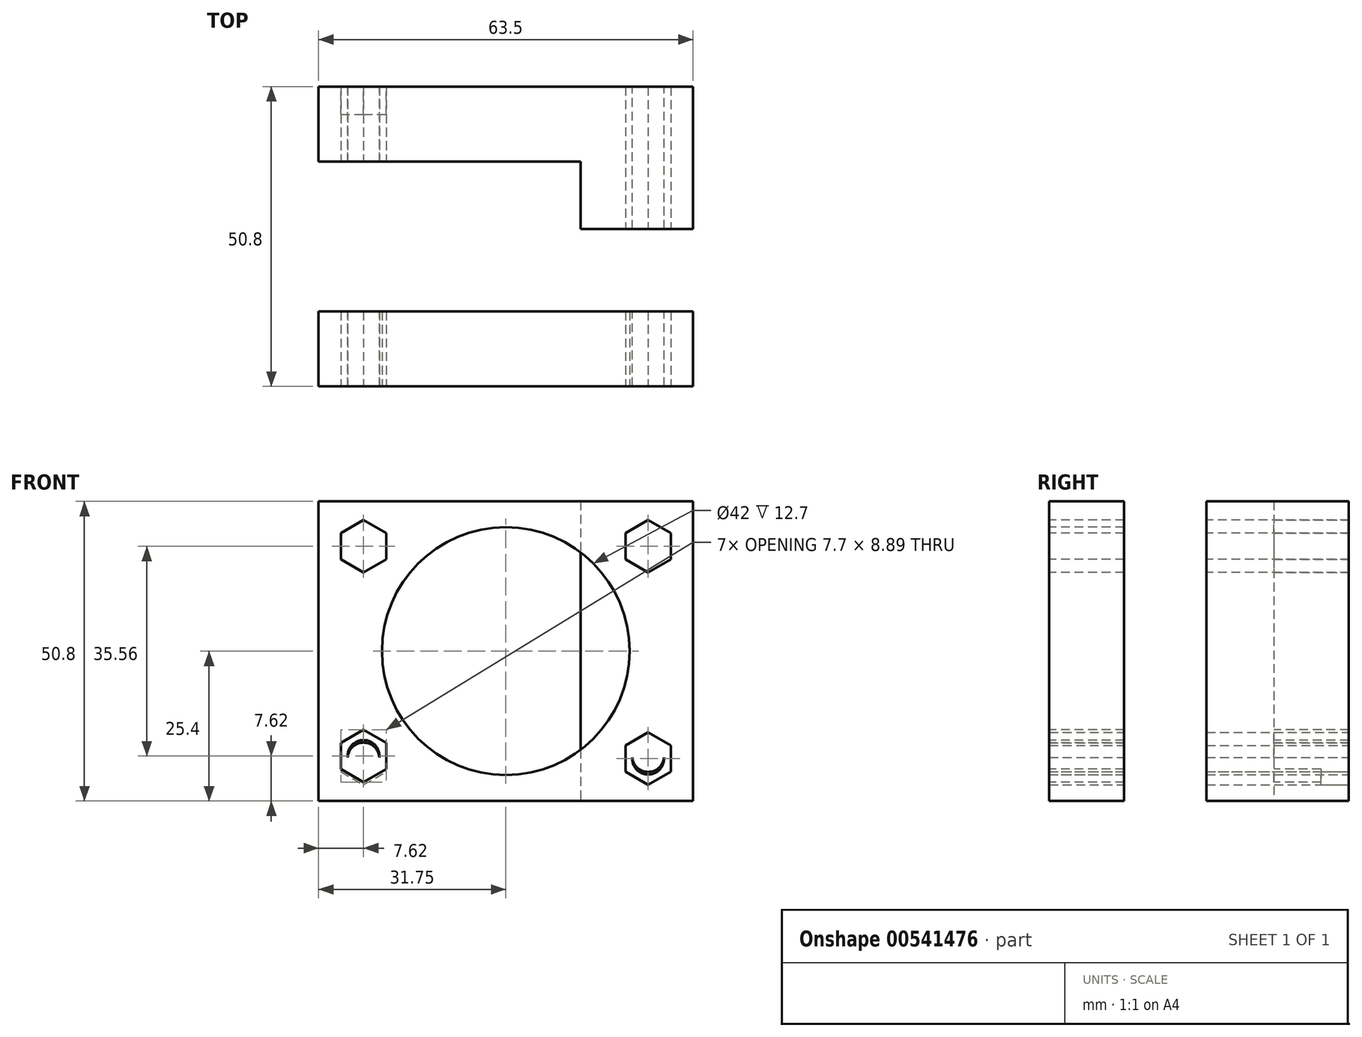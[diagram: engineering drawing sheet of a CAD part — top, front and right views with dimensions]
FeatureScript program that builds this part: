
annotation { "Feature Type Name" : "Feature", "Feature Type Description" : "" }
export const myFeature = defineFeature(function(context is Context, id is Id, definition is map)
    precondition{}
    {
        {
            var Q0;
            Q0=qCreatedBy(makeId("Top.planeOp"),FACE);
            var sketch = newSketch(context, id + "F0", { "sketchPlane" : qUnion([Q0])});
            skLineSegment(sketch, "E0.bottom", {"start": v(0, 0) * mm, "end": v(63.5, 0) * mm});
            skLineSegment(sketch, "E0.top", {"start": v(0, 12.7) * mm, "end": v(63.5, 12.7) * mm});
            skLineSegment(sketch, "E0.left", {"start": v(0, 0) * mm, "end": v(0, 12.7) * mm});
            skLineSegment(sketch, "E0.right", {"start": v(63.5, 0) * mm, "end": v(63.5, 12.7) * mm});
            skLineSegment(sketch, "E1.bottom", {"start": v(0, 12.7) * mm, "end": v(19.05, 12.7) * mm});
            skLineSegment(sketch, "E1.top", {"start": v(0, 24.13) * mm, "end": v(19.05, 24.13) * mm});
            skLineSegment(sketch, "E1.left", {"start": v(0, 12.7) * mm, "end": v(0, 24.13) * mm});
            skLineSegment(sketch, "E1.right", {"start": v(19.05, 12.7) * mm, "end": v(19.05, 24.13) * mm});
            skLineSegment(sketch, "E2.bottom", {"start": v(63.5, 12.7) * mm, "end": v(44.45, 12.7) * mm});
            skLineSegment(sketch, "E2.top", {"start": v(63.5, 24.13) * mm, "end": v(44.45, 24.13) * mm});
            skLineSegment(sketch, "E2.left", {"start": v(63.5, 12.7) * mm, "end": v(63.5, 24.13) * mm});
            skLineSegment(sketch, "E2.right", {"start": v(44.45, 12.7) * mm, "end": v(44.45, 24.13) * mm});
            skLineSegment(sketch, "E3", {"start": v(25.4, 25.4) * mm, "end": v(0, 25.4) * mm});
            skLineSegment(sketch, "E4.MirrorCS", {"start": v(0, 50.8) * mm, "end": v(0, 38.1) * mm});
            skLineSegment(sketch, "E5.MirrorCS", {"start": v(44.45, 38.1) * mm, "end": v(44.45, 26.67) * mm});
            skLineSegment(sketch, "E6.MirrorCS", {"start": v(63.5, 38.1) * mm, "end": v(63.5, 26.67) * mm});
            skLineSegment(sketch, "E7.MirrorCS", {"start": v(63.5, 26.67) * mm, "end": v(44.45, 26.67) * mm});
            skLineSegment(sketch, "E8.MirrorCS", {"start": v(63.5, 38.1) * mm, "end": v(44.45, 38.1) * mm});
            skLineSegment(sketch, "E9.MirrorCS", {"start": v(0, 50.8) * mm, "end": v(63.5, 50.8) * mm});
            skLineSegment(sketch, "E10.MirrorCS", {"start": v(0, 38.1) * mm, "end": v(63.5, 38.1) * mm});
            skLineSegment(sketch, "E11.MirrorCS", {"start": v(63.5, 50.8) * mm, "end": v(63.5, 38.1) * mm});
            skLineSegment(sketch, "E12.MirrorCS", {"start": v(0, 38.1) * mm, "end": v(19.05, 38.1) * mm});
            skLineSegment(sketch, "E13.MirrorCS", {"start": v(0, 26.67) * mm, "end": v(19.05, 26.67) * mm});
            skLineSegment(sketch, "E14.MirrorCS", {"start": v(0, 38.1) * mm, "end": v(0, 26.67) * mm});
            skLineSegment(sketch, "E15.MirrorCS", {"start": v(19.05, 38.1) * mm, "end": v(19.05, 26.67) * mm});
            skPoint(sketch, "E16.orphan", {"position": v(25.4, 25.4) * mm});
            skPoint(sketch, "E17.MirrorCS.start.orphan", {"position": v(31.75, 50.8) * mm});
            skPoint(sketch, "E18.start.orphan", {"position": v(31.75, 0) * mm});
            skSolve(sketch);
        }
        {
            var Q0;
            Q0=makeQuery(id+"F0.imprint","IMPRINT",FACE,{"disambiguationData":[TD([[makeQuery(id+"F0.imprint","IMPRINT",EDGE,{"derivedFrom":sQuery(id+"F0.wireOp",EDGE,"E4.MirrorCS")}),1.0]])]});
            var Q1;
            Q1=makeQuery(id+"F0.imprint","IMPRINT",FACE,{"disambiguationData":[TD([[makeQuery(id+"F0.imprint","IMPRINT",EDGE,{"derivedFrom":sQuery(id+"F0.wireOp",EDGE,"E12.MirrorCS")}),-1.0]])]});
            var Q2;
            {var subQ0=sQuery(id+"F0.wireOp",EDGE,"E5.MirrorCS");Q2=makeQuery(id+"F0.imprint","IMPRINT",FACE,{"disambiguationData":[TD([[makeQuery(id+"F0.imprint","IMPRINT",EDGE,{"derivedFrom":subQ0}),1.0]])]});}
            var Q3;
            Q3=makeQuery(id+"F0.imprint","IMPRINT",FACE,{"disambiguationData":[TD([[makeQuery(id+"F0.imprint","IMPRINT",EDGE,{"derivedFrom":sQuery(id+"F0.wireOp",EDGE,"E2.bottom")}),-1.0]])]});
            var Q4;
            Q4=makeQuery(id+"F0.imprint","IMPRINT",FACE,{"disambiguationData":[TD([[makeQuery(id+"F0.imprint","IMPRINT",EDGE,{"derivedFrom":sQuery(id+"F0.wireOp",EDGE,"E0.bottom")}),1.0]])]});
            var Q5;
            Q5=makeQuery(id+"F0.imprint","IMPRINT",FACE,{"disambiguationData":[TD([[makeQuery(id+"F0.imprint","IMPRINT",EDGE,{"derivedFrom":sQuery(id+"F0.wireOp",EDGE,"E1.bottom")}),1.0]])]});
            extrude(context, id + "F1", {"entities" : qUnion([Q0, Q1, Q2, Q3, Q4, Q5]), "depth" : 50.8 * mm, "offsetDistance" : 25.4 * mm});
        }
        {
            var Q0;
            Q0=makeQuery(id+"F1.opExtrude","SWEPT_FACE",FACE,{"disambiguationData":[OSD([sQuery(id+"F0.wireOp",EDGE,"E0.bottom")])]});
            var sketch = newSketch(context, id + "F2", { "sketchPlane" : qUnion([Q0])});
            skCircle(sketch, "E19", {"center": v(31.75, 25.4) * mm, "radius": 21 * mm});
            skPoint(sketch, "E19.centerSnap0", {"position": v(0, 25.4) * mm});
            skPoint(sketch, "E19.centerSnap1", {"position": v(31.75, 50.8) * mm});
            skLineSegment(sketch, "E20", {"start": v(0, 50.8) * mm, "end": v(7.62, 50.8) * mm});
            skLineSegment(sketch, "E21", {"start": v(0, 50.8) * mm, "end": v(0, 43.18) * mm});
            skCircle(sketch, "E22", {"center": v(7.62, 43.18) * mm, "radius": 2.7 * mm});
            skLineSegment(sketch, "E23", {"start": v(7.62, 43.18) * mm, "end": v(7.62, 38.74) * mm});
            skCircle(sketch, "E24.cCircle", {"center": v(7.62, 43.18) * mm, "radius": 4.44 * mm, "construction": true});
            skLineSegment(sketch, "E24.0", {"start": v(7.62, 38.74) * mm, "end": v(3.77, 40.96) * mm});
            skLineSegment(sketch, "E24.1", {"start": v(3.77, 40.96) * mm, "end": v(3.77, 45.4) * mm});
            skLineSegment(sketch, "E24.2", {"start": v(3.77, 45.4) * mm, "end": v(7.62, 47.62) * mm});
            skLineSegment(sketch, "E24.3", {"start": v(7.62, 47.62) * mm, "end": v(11.47, 45.4) * mm});
            skLineSegment(sketch, "E24.4", {"start": v(11.47, 45.4) * mm, "end": v(11.47, 40.96) * mm});
            skLineSegment(sketch, "E24.5", {"start": v(11.47, 40.96) * mm, "end": v(7.62, 38.74) * mm});
            skLineSegment(sketch, "E25", {"start": v(0, 25.4) * mm, "end": v(2.5, 25.4) * mm});
            skLineSegment(sketch, "E26", {"start": v(31.75, 50.8) * mm, "end": v(31.75, 48.56) * mm});
            skLineSegment(sketch, "E27.MirrorCS", {"start": v(3.77, 5.4) * mm, "end": v(7.62, 3.18) * mm});
            skLineSegment(sketch, "E28.MirrorCS", {"start": v(7.62, 12.07) * mm, "end": v(3.77, 9.84) * mm});
            skCircle(sketch, "E29.MirrorC", {"center": v(7.62, 7.62) * mm, "radius": 2.7 * mm});
            skLineSegment(sketch, "E30.MirrorCS", {"start": v(11.47, 9.84) * mm, "end": v(7.62, 12.07) * mm});
            skLineSegment(sketch, "E31.MirrorCS", {"start": v(7.62, 3.18) * mm, "end": v(11.47, 5.4) * mm});
            skCircle(sketch, "E32.MirrorC", {"center": v(7.62, 7.62) * mm, "radius": 4.44 * mm, "construction": true});
            skLineSegment(sketch, "E33.MirrorCS", {"start": v(7.62, 7.62) * mm, "end": v(7.62, 12.07) * mm});
            skLineSegment(sketch, "E34.MirrorCS", {"start": v(11.47, 5.4) * mm, "end": v(11.47, 9.84) * mm});
            skLineSegment(sketch, "E35.MirrorCS", {"start": v(3.77, 9.84) * mm, "end": v(3.77, 5.4) * mm});
            skLineSegment(sketch, "E36.MirrorCS", {"start": v(59.73, 45.4) * mm, "end": v(55.88, 47.62) * mm});
            skLineSegment(sketch, "E37.MirrorCS", {"start": v(55.88, 38.74) * mm, "end": v(59.73, 40.96) * mm});
            skCircle(sketch, "E38.MirrorC", {"center": v(55.88, 43.18) * mm, "radius": 4.44 * mm, "construction": true});
            skLineSegment(sketch, "E39.MirrorCS", {"start": v(55.88, 43.18) * mm, "end": v(55.88, 38.74) * mm});
            skCircle(sketch, "E40.MirrorC", {"center": v(55.88, 43.18) * mm, "radius": 2.7 * mm});
            skLineSegment(sketch, "E41.MirrorCS", {"start": v(59.73, 40.96) * mm, "end": v(59.73, 45.4) * mm});
            skLineSegment(sketch, "E42.MirrorCS", {"start": v(55.88, 47.62) * mm, "end": v(52.03, 45.4) * mm});
            skLineSegment(sketch, "E43.MirrorCS", {"start": v(52.03, 40.96) * mm, "end": v(55.88, 38.74) * mm});
            skLineSegment(sketch, "E44.MirrorCS", {"start": v(55.88, 3.18) * mm, "end": v(52.03, 5.4) * mm});
            skLineSegment(sketch, "E45.MirrorCS", {"start": v(55.88, 12.07) * mm, "end": v(59.73, 9.84) * mm});
            skCircle(sketch, "E46.MirrorC", {"center": v(55.88, 7.62) * mm, "radius": 2.7 * mm});
            skLineSegment(sketch, "E47.MirrorCS", {"start": v(59.73, 5.4) * mm, "end": v(55.88, 3.18) * mm});
            skLineSegment(sketch, "E48.MirrorCS", {"start": v(52.03, 9.84) * mm, "end": v(55.88, 12.07) * mm});
            skCircle(sketch, "E49.MirrorC", {"center": v(55.88, 7.62) * mm, "radius": 4.44 * mm, "construction": true});
            skLineSegment(sketch, "E50.MirrorCS", {"start": v(55.88, 7.62) * mm, "end": v(55.88, 12.07) * mm});
            skLineSegment(sketch, "E51.MirrorCS", {"start": v(59.73, 9.84) * mm, "end": v(59.73, 5.4) * mm});
            skLineSegment(sketch, "E52.MirrorCS", {"start": v(52.03, 5.4) * mm, "end": v(52.03, 9.84) * mm});
            skLineSegment(sketch, "E53.MirrorCS", {"start": v(52.03, 45.4) * mm, "end": v(52.03, 40.96) * mm});
            skSolve(sketch);
        }
        {
            var Q0;
            Q0=makeQuery(id+"F2.imprint","IMPRINT",FACE,{"disambiguationData":[TD([[makeQuery(id+"F2.imprint","IMPRINT",EDGE,{"derivedFrom":sQuery(id+"F2.wireOp",EDGE,"E22")}),1.0]])]});
            var Q1;
            Q1=makeQuery(id+"F2.imprint","IMPRINT",FACE,{"disambiguationData":[TD([[makeQuery(id+"F2.imprint","IMPRINT",EDGE,{"derivedFrom":sQuery(id+"F2.wireOp",EDGE,"E29.MirrorC")}),-1.0]])]});
            var Q2;
            Q2=makeQuery(id+"F2.imprint","IMPRINT",FACE,{"disambiguationData":[TD([[makeQuery(id+"F2.imprint","IMPRINT",EDGE,{"derivedFrom":sQuery(id+"F2.wireOp",EDGE,"E46.MirrorC")}),1.0]])]});
            var Q3;
            Q3=makeQuery(id+"F2.imprint","IMPRINT",FACE,{"disambiguationData":[TD([[makeQuery(id+"F2.imprint","IMPRINT",EDGE,{"derivedFrom":sQuery(id+"F2.wireOp",EDGE,"E40.MirrorC")}),-1.0]])]});
            extrude(context, id + "F3", {"entities" : qUnion([Q0, Q1, Q2, Q3]), "operationType" : NewBodyOperationType.REMOVE, "oppositeDirection" : true, "depth" : 50.8 * mm, "offsetDistance" : 25.4 * mm});
        }
        {
            var Q0;
            Q0=makeQuery(id+"F2.imprint","IMPRINT",FACE,{"disambiguationData":[TD([[makeQuery(id+"F2.imprint","IMPRINT",EDGE,{"derivedFrom":sQuery(id+"F2.wireOp",EDGE,"E19")}),1.0]])]});
            extrude(context, id + "F4", {"entities" : qUnion([Q0]), "operationType" : NewBodyOperationType.REMOVE, "oppositeDirection" : true, "depth" : 12.7 * mm, "offsetDistance" : 25.4 * mm});
        }
        {
            var Q0;
            Q0=makeQuery(id+"F1.opExtrude","SWEPT_FACE",FACE,{"disambiguationData":[OSD([sQuery(id+"F0.wireOp",EDGE,"E9.MirrorCS")])]});
            var sketch = newSketch(context, id + "F5", { "sketchPlane" : qUnion([Q0])});
            skCircle(sketch, "E54", {"center": v(-31.75, 25.18) * mm, "radius": 21 * mm});
            skPoint(sketch, "E54.centerSnap0", {"position": v(-68.13, 25.18) * mm});
            skPoint(sketch, "E54.centerSnap1", {"position": v(-31.75, 50.8) * mm});
            skLineSegment(sketch, "E55", {"start": v(-63.5, 50.8) * mm, "end": v(-55.88, 50.8) * mm});
            skLineSegment(sketch, "E56", {"start": v(-63.5, 50.8) * mm, "end": v(-63.5, 43.18) * mm});
            skCircle(sketch, "E57", {"center": v(-55.88, 43.18) * mm, "radius": 2.7 * mm});
            skLineSegment(sketch, "E58", {"start": v(-55.88, 43.18) * mm, "end": v(-55.88, 38.74) * mm});
            skCircle(sketch, "E59.cCircle", {"center": v(-55.88, 43.18) * mm, "radius": 4.44 * mm, "construction": true});
            skLineSegment(sketch, "E59.0", {"start": v(-55.88, 38.74) * mm, "end": v(-59.73, 40.96) * mm});
            skLineSegment(sketch, "E59.1", {"start": v(-59.73, 40.96) * mm, "end": v(-59.73, 45.4) * mm});
            skLineSegment(sketch, "E59.2", {"start": v(-59.73, 45.4) * mm, "end": v(-55.88, 47.62) * mm});
            skLineSegment(sketch, "E59.3", {"start": v(-55.88, 47.62) * mm, "end": v(-52.03, 45.4) * mm});
            skLineSegment(sketch, "E59.4", {"start": v(-52.03, 45.4) * mm, "end": v(-52.03, 40.96) * mm});
            skLineSegment(sketch, "E59.5", {"start": v(-52.03, 40.96) * mm, "end": v(-55.88, 38.74) * mm});
            skLineSegment(sketch, "E60", {"start": v(-68.13, 25.18) * mm, "end": v(-65.62, 25.18) * mm});
            skLineSegment(sketch, "E61", {"start": v(-31.75, 50.8) * mm, "end": v(-31.75, 48.56) * mm});
            skLineSegment(sketch, "E62.MirrorCS", {"start": v(-59.73, 4.96) * mm, "end": v(-55.88, 2.74) * mm});
            skLineSegment(sketch, "E63.MirrorCS", {"start": v(-55.88, 11.63) * mm, "end": v(-59.73, 9.4) * mm});
            skCircle(sketch, "E64.MirrorC", {"center": v(-55.88, 7.18) * mm, "radius": 2.7 * mm});
            skLineSegment(sketch, "E65.MirrorCS", {"start": v(-52.03, 9.4) * mm, "end": v(-55.88, 11.63) * mm});
            skLineSegment(sketch, "E66.MirrorCS", {"start": v(-55.88, 2.74) * mm, "end": v(-52.03, 4.96) * mm});
            skCircle(sketch, "E67.MirrorC", {"center": v(-55.88, 7.18) * mm, "radius": 4.44 * mm, "construction": true});
            skLineSegment(sketch, "E68.MirrorCS", {"start": v(-55.88, 7.18) * mm, "end": v(-55.88, 11.63) * mm});
            skLineSegment(sketch, "E69.MirrorCS", {"start": v(-52.03, 4.96) * mm, "end": v(-52.03, 9.4) * mm});
            skLineSegment(sketch, "E70.MirrorCS", {"start": v(-59.73, 9.4) * mm, "end": v(-59.73, 4.96) * mm});
            skLineSegment(sketch, "E71.MirrorCS", {"start": v(-3.77, 45.4) * mm, "end": v(-7.62, 47.62) * mm});
            skLineSegment(sketch, "E72.MirrorCS", {"start": v(-7.62, 38.73) * mm, "end": v(-3.77, 40.96) * mm});
            skCircle(sketch, "E73.MirrorC", {"center": v(-7.62, 43.18) * mm, "radius": 4.44 * mm, "construction": true});
            skLineSegment(sketch, "E74.MirrorCS", {"start": v(-7.62, 43.18) * mm, "end": v(-7.62, 38.73) * mm});
            skCircle(sketch, "E75.MirrorC", {"center": v(-7.62, 43.18) * mm, "radius": 2.7 * mm});
            skLineSegment(sketch, "E76.MirrorCS", {"start": v(-3.77, 40.96) * mm, "end": v(-3.77, 45.4) * mm});
            skLineSegment(sketch, "E77.MirrorCS", {"start": v(-7.62, 47.62) * mm, "end": v(-11.47, 45.4) * mm});
            skLineSegment(sketch, "E78.MirrorCS", {"start": v(-11.47, 40.96) * mm, "end": v(-7.62, 38.74) * mm});
            skLineSegment(sketch, "E79.MirrorCS", {"start": v(-7.62, 2.74) * mm, "end": v(-11.47, 4.96) * mm});
            skLineSegment(sketch, "E80.MirrorCS", {"start": v(-7.62, 11.63) * mm, "end": v(-3.77, 9.4) * mm});
            skCircle(sketch, "E81.MirrorC", {"center": v(-7.62, 7.18) * mm, "radius": 2.7 * mm});
            skLineSegment(sketch, "E82.MirrorCS", {"start": v(-3.77, 4.96) * mm, "end": v(-7.62, 2.74) * mm});
            skLineSegment(sketch, "E83.MirrorCS", {"start": v(-11.47, 9.4) * mm, "end": v(-7.62, 11.63) * mm});
            skCircle(sketch, "E84.MirrorC", {"center": v(-7.62, 7.18) * mm, "radius": 4.44 * mm, "construction": true});
            skLineSegment(sketch, "E85.MirrorCS", {"start": v(-7.62, 7.18) * mm, "end": v(-7.62, 11.63) * mm});
            skLineSegment(sketch, "E86.MirrorCS", {"start": v(-3.77, 9.4) * mm, "end": v(-3.77, 4.96) * mm});
            skLineSegment(sketch, "E87.MirrorCS", {"start": v(-11.47, 4.96) * mm, "end": v(-11.47, 9.4) * mm});
            skLineSegment(sketch, "E88.MirrorCS", {"start": v(-11.47, 45.4) * mm, "end": v(-11.47, 40.96) * mm});
            skLineSegment(sketch, "E89", {"start": v(-55.88, 50.8) * mm, "end": v(-55.88, 43.18) * mm});
            skSolve(sketch);
        }
        {
            var Q0;
            Q0=makeQuery(id+"F5.imprint","IMPRINT",FACE,{"disambiguationData":[TD([[makeQuery(id+"F5.imprint","IMPRINT",EDGE,{"derivedFrom":sQuery(id+"F5.wireOp",EDGE,"E57")}),1.0]])]});
            var Q1;
            Q1=makeQuery(id+"F5.imprint","IMPRINT",FACE,{"disambiguationData":[TD([[makeQuery(id+"F5.imprint","IMPRINT",EDGE,{"derivedFrom":sQuery(id+"F5.wireOp",EDGE,"E75.MirrorC")}),-1.0]])]});
            var Q2;
            Q2=makeQuery(id+"F5.imprint","IMPRINT",FACE,{"disambiguationData":[TD([[makeQuery(id+"F5.imprint","IMPRINT",EDGE,{"derivedFrom":sQuery(id+"F5.wireOp",EDGE,"E81.MirrorC")}),1.0]])]});
            var Q3;
            Q3=makeQuery(id+"F5.imprint","IMPRINT",FACE,{"disambiguationData":[TD([[makeQuery(id+"F5.imprint","IMPRINT",EDGE,{"derivedFrom":sQuery(id+"F5.wireOp",EDGE,"E64.MirrorC")}),-1.0]])]});
            extrude(context, id + "F6", {"entities" : qUnion([Q0, Q1, Q2, Q3]), "operationType" : NewBodyOperationType.REMOVE, "oppositeDirection" : true, "depth" : 50.8 * mm, "offsetDistance" : 25.4 * mm});
        }
        {
            var Q0;
            Q0=makeQuery(id+"F5.imprint","IMPRINT",FACE,{"disambiguationData":[TD([[makeQuery(id+"F5.imprint","IMPRINT",EDGE,{"derivedFrom":sQuery(id+"F5.wireOp",EDGE,"E62.MirrorCS")}),1.0]])]});
            var Q1;
            Q1=makeQuery(id+"F5.imprint","IMPRINT",FACE,{"disambiguationData":[TD([[makeQuery(id+"F5.imprint","IMPRINT",EDGE,{"derivedFrom":sQuery(id+"F5.wireOp",EDGE,"E79.MirrorCS")}),-1.0]])]});
            var Q2;
            Q2=makeQuery(id+"F5.imprint","IMPRINT",FACE,{"disambiguationData":[TD([[makeQuery(id+"F5.imprint","IMPRINT",EDGE,{"derivedFrom":sQuery(id+"F5.wireOp",EDGE,"E71.MirrorCS")}),1.0]])]});
            var Q3;
            {var subQ0=sQuery(id+"F5.wireOp",EDGE,"E59.3");Q3=makeQuery(id+"F5.imprint","IMPRINT",FACE,{"disambiguationData":[TD([[makeQuery(id+"F5.imprint","IMPRINT",EDGE,{"derivedFrom":subQ0}),-1.0]])]});}
            var Q4;
            {var subQ0=sQuery(id+"F5.wireOp",EDGE,"E59.0");Q4=makeQuery(id+"F5.imprint","IMPRINT",FACE,{"disambiguationData":[TD([[makeQuery(id+"F5.imprint","IMPRINT",EDGE,{"derivedFrom":subQ0}),-1.0]])]});}
            extrude(context, id + "F7", {"entities" : qUnion([Q0, Q1, Q2, Q3, Q4]), "operationType" : NewBodyOperationType.REMOVE, "oppositeDirection" : true, "depth" : 4.7 * mm, "offsetDistance" : 25.4 * mm});
        }
    });
